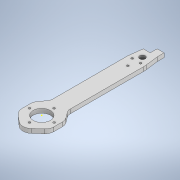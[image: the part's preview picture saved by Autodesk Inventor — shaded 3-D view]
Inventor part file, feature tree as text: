
AUTODESK INVENTOR PART (.ipt)
format: ipt  version: 2020 (Build 240168000, 168)  size: 289,792 bytes
history: native  units: in
note: dims shown in document units (in); Inventor stores cm internally (conversion verified against a paired STEP export)
features: sketch x5, extrude x4, projected_geometry x2, fillet x1
ambient origin geometry x8: Origin, YZ Plane, XZ Plane, XY Plane, X Axis, Y Axis, Z Axis, Center Point
bodies: Solid1 (feature_tree)
feature tree (12):
  extrude  "Extrusion1"  Depth=0.2362in
  extrude  "Extrusion2"  Depth=0.3937in
  sketch  "Sketch3"  dims[d9=0.2362in d10=0.0in d11=0.1181in]
  fillet  "Fillet1"  Radius=0.2362in
  extrude  "Extrusion3"  Depth=0.2362in
  extrude  "Extrusion4"  Depth=0.2362in TaperAngle=0.0deg
  sketch  "Sketch5"
  sketch  "Sketch1"  dims[d0=0.2362in d1=0.0in d2=0.1181in]
  sketch  "Sketch2"  dims[d3=0.2362in d4=0.0in d7=0.3937in d8=0.2362in]
  projected_geometry  "Projected Loop1"
  projected_geometry  "Projected Loop2"
  sketch  "Sketch4"  dims[d12=1.5748in d14=360.0deg d16=0.2362in d17=0.0in]
